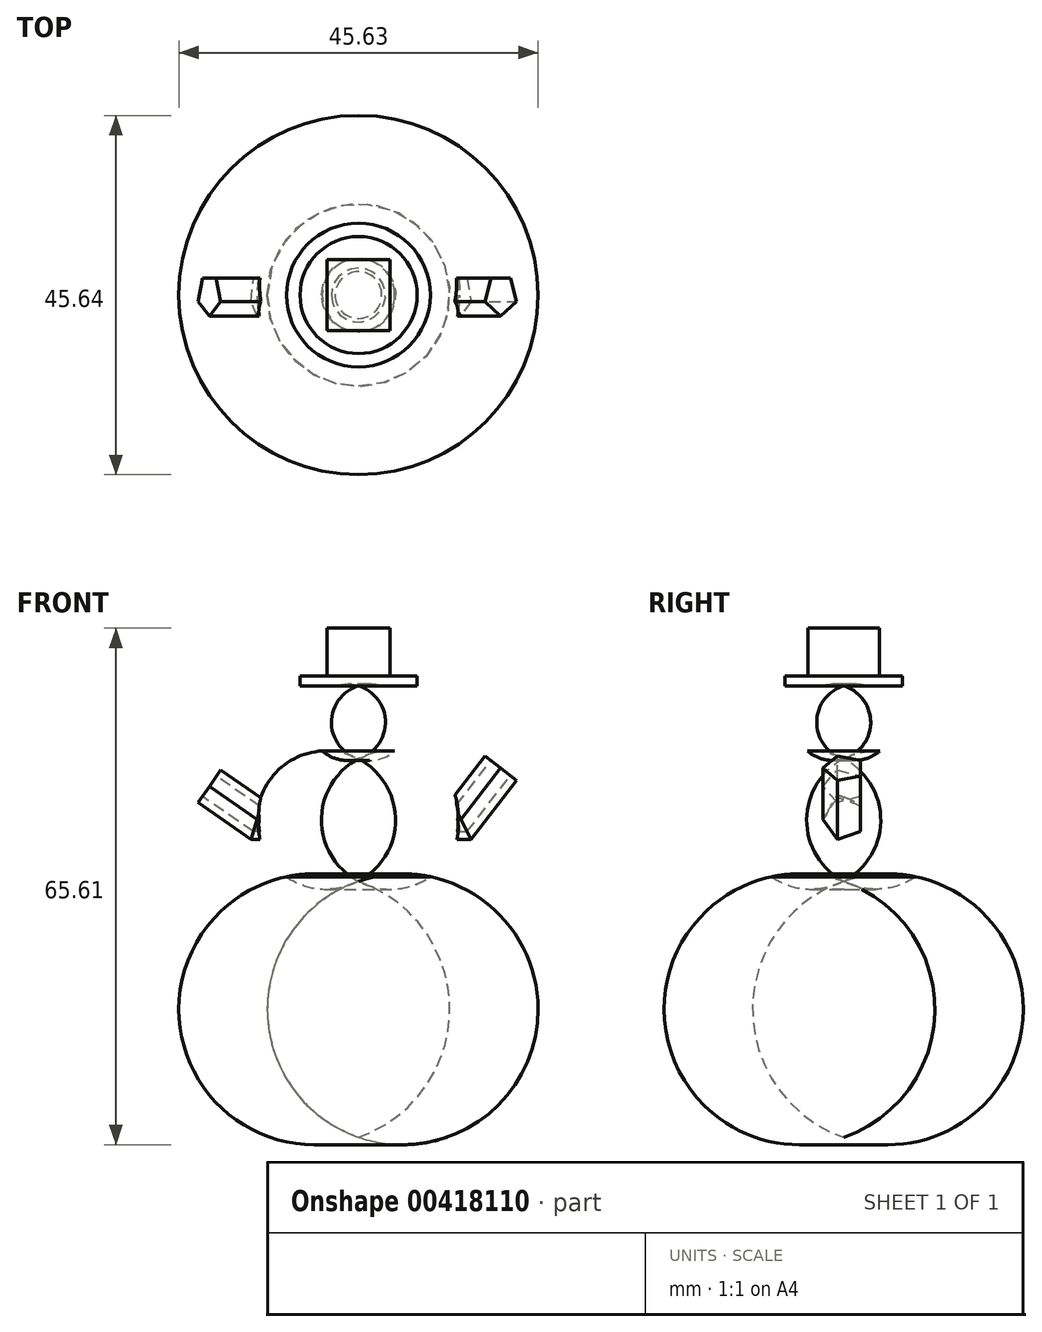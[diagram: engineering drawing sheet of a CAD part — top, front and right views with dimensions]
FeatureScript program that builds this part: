
annotation { "Feature Type Name" : "Feature", "Feature Type Description" : "" }
export const myFeature = defineFeature(function(context is Context, id is Id, definition is map)
    precondition{}
    {
        {
            var Q0;
            Q0=qCreatedBy(makeId("Front.planeOp"),FACE);
            var sketch = newSketch(context, id + "F0", { "sketchPlane" : qUnion([Q0])});
            skLineSegment(sketch, "E0", {"start": v(-0.02, 0.05) * mm, "end": v(-0.02, -57.3) * mm});
            skArc(sketch, "E1", {"start": v(-0.02, 0.05) * mm, "mid": v(-6.28, -4.58) * mm, "end": v(-0.02, -9.21) * mm});
            skArc(sketch, "E2", {"start": v(-0.02, -9.21) * mm, "mid": v(6.23, -4.58) * mm, "end": v(-0.02, 0.05) * mm});
            skArc(sketch, "E3", {"start": v(-0.02, -9.21) * mm, "mid": v(-12.84, -17) * mm, "end": v(-0.02, -24.78) * mm});
            skArc(sketch, "E4", {"start": v(-0.02, -24.78) * mm, "mid": v(12.86, -17) * mm, "end": v(-0.02, -9.21) * mm});
            skArc(sketch, "E5", {"start": v(-0.02, -24.78) * mm, "mid": v(-22.98, -41.04) * mm, "end": v(-0.02, -57.3) * mm});
            skArc(sketch, "E6", {"start": v(-0.02, -57.3) * mm, "mid": v(22.8, -41.04) * mm, "end": v(-0.02, -24.78) * mm});
            skSolve(sketch);
        }
        {
            var Q0;
            {var subQ0=sQuery(id+"F0.wireOp",EDGE,"E4");var subQ2=sQuery(id+"F0.wireOp",EDGE,"E2");var subQ7=makeQuery(id+"F0.imprint","INTERSECT",VERTEX,{"derivedFrom":[subQ2,subQ0]});Q0=makeQuery(id+"F0.imprint","IMPRINT",FACE,{"disambiguationData":[TD([[makeQuery(id+"F0.imprint","IMPRINT",EDGE,{"disambiguationData":[TD([[subQ7,1.0]])],"derivedFrom":subQ0}),1.0]])]});}
            var Q1;
            Q1=sQuery(id+"F0.wireOp",EDGE,"E0");
            revolve(context, id + "F1", {"entities" : qUnion([Q0]), "axis" : qUnion([Q1]), "revolveType" : RevolveType.FULL});
        }
        {
            var Q0;
            {var subQ0=sQuery(id+"F0.wireOp",EDGE,"E2");var subQ4=sQuery(id+"F0.wireOp",EDGE,"E4");var subQ6=makeQuery(id+"F0.imprint","INTERSECT",VERTEX,{"derivedFrom":[subQ0,subQ4]});Q0=makeQuery(id+"F0.imprint","IMPRINT",FACE,{"disambiguationData":[TD([[makeQuery(id+"F0.imprint","IMPRINT",EDGE,{"disambiguationData":[TD([[subQ6,-1.0]])],"derivedFrom":subQ0}),1.0]])]});}
            var Q1;
            Q1=sQuery(id+"F0.wireOp",EDGE,"E0");
            revolve(context, id + "F2", {"entities" : qUnion([Q0]), "axis" : qUnion([Q1]), "revolveType" : RevolveType.FULL});
        }
        {
            var Q0;
            {var subQ0=sQuery(id+"F0.wireOp",EDGE,"E6");var subQ4=sQuery(id+"F0.wireOp",EDGE,"E4");var subQ6=makeQuery(id+"F0.imprint","INTERSECT",VERTEX,{"derivedFrom":[subQ4,subQ0]});Q0=makeQuery(id+"F0.imprint","IMPRINT",FACE,{"disambiguationData":[TD([[makeQuery(id+"F0.imprint","IMPRINT",EDGE,{"disambiguationData":[TD([[subQ6,1.0]])],"derivedFrom":subQ0}),1.0]])]});}
            var Q1;
            {var subQ0=sQuery(id+"F0.wireOp",EDGE,"E6");var subQ1=sQuery(id+"F0.wireOp",EDGE,"E4");var subQ3=makeQuery(id+"F0.imprint","INTERSECT",VERTEX,{"derivedFrom":[subQ1,subQ0]});Q1=makeQuery(id+"F0.imprint","IMPRINT",FACE,{"disambiguationData":[TD([[makeQuery(id+"F0.imprint","IMPRINT",EDGE,{"disambiguationData":[TD([[subQ3,1.0]])],"derivedFrom":subQ1}),1.0]])]});}
            var Q2;
            Q2=sQuery(id+"F0.wireOp",EDGE,"E0");
            revolve(context, id + "F3", {"entities" : qUnion([Q0, Q1]), "axis" : qUnion([Q2]), "revolveType" : RevolveType.FULL});
        }
        {
            var Q0;
            Q0=qCreatedBy(makeId("Top.planeOp"),FACE);
            var sketch = newSketch(context, id + "F4", { "sketchPlane" : qUnion([Q0])});
            skCircle(sketch, "E7", {"center": v(0, 0) * mm, "radius": 7.43 * mm});
            skSolve(sketch);
        }
        {
            var Q0;
            Q0=makeQuery(id+"F4.imprint","IMPRINT",FACE,{"disambiguationData":[TD([[makeQuery(id+"F4.imprint","IMPRINT",EDGE,{"derivedFrom":sQuery(id+"F4.wireOp",EDGE,"E7")}),1.0]])]});
            extrude(context, id + "F5", {"entities" : qUnion([Q0]), "operationType" : NewBodyOperationType.ADD, "depth" : 1.27 * mm});
        }
        {
            var Q0;
            Q0=qCreatedBy(makeId("Front.planeOp"),FACE);
            var sketch = newSketch(context, id + "F6", { "sketchPlane" : qUnion([Q0])});
            skLineSegment(sketch, "E8", {"start": v(0, -16.92) * mm, "end": v(-12.88, -16.92) * mm});
            skLineSegment(sketch, "E9", {"start": v(-12.88, -16.92) * mm, "end": v(-18.97, -12.71) * mm});
            skSolve(sketch);
        }
        {
            var Q0;
            Q0=qCreatedBy(makeId("Front.planeOp"),FACE);
            var sketch = newSketch(context, id + "F7", { "sketchPlane" : qUnion([Q0])});
            skLineSegment(sketch, "E10", {"start": v(0, -16.9) * mm, "end": v(13, -16.9) * mm});
            skLineSegment(sketch, "E11", {"start": v(13, -16.9) * mm, "end": v(18.02, -10.41) * mm});
            skSolve(sketch);
        }
        {
            var Q0;
            Q0=makeQuery(id+"F5.opExtrude","CAP_FACE",FACE,{"disambiguationData":[OSD([sQuery(id+"F4.wireOp",EDGE,"E7")])],"isStart":false});
            var sketch = newSketch(context, id + "F8", { "sketchPlane" : qUnion([Q0])});
            skLineSegment(sketch, "E12.bottom", {"start": v(3.99, -4.53) * mm, "end": v(-3.99, -4.53) * mm});
            skLineSegment(sketch, "E12.top", {"start": v(3.99, 4.53) * mm, "end": v(-3.99, 4.53) * mm});
            skLineSegment(sketch, "E12.left", {"start": v(3.99, -4.53) * mm, "end": v(3.99, 4.53) * mm});
            skLineSegment(sketch, "E12.right", {"start": v(-3.99, -4.53) * mm, "end": v(-3.99, 4.53) * mm});
            skPoint(sketch, "E12.middle", {"position": v(0, 0) * mm});
            skSolve(sketch);
        }
        {
            var Q0;
            Q0=makeQuery(id+"F8.imprint","IMPRINT",FACE,{"disambiguationData":[TD([[makeQuery(id+"F8.imprint","IMPRINT",EDGE,{"derivedFrom":sQuery(id+"F8.wireOp",EDGE,"E12.bottom")}),-1.0]])]});
            extrude(context, id + "F9", {"entities" : qUnion([Q0]), "operationType" : NewBodyOperationType.ADD, "depth" : 6.1 * mm});
        }
        {
            var Q0;
            Q0=qCreatedBy(makeId("Right.planeOp"),FACE);
            var sketch = newSketch(context, id + "F10", { "sketchPlane" : qUnion([Q0])});
            skCircle(sketch, "E13.cCircle", {"center": v(0, -16.91) * mm, "radius": 2.15 * mm, "construction": true});
            skLineSegment(sketch, "E13.0", {"start": v(2.15, -15.35) * mm, "end": v(2.15, -18.47) * mm});
            skLineSegment(sketch, "E13.1", {"start": v(2.15, -18.47) * mm, "end": v(-0.82, -19.44) * mm});
            skLineSegment(sketch, "E13.2", {"start": v(-0.82, -19.44) * mm, "end": v(-2.66, -16.91) * mm});
            skLineSegment(sketch, "E13.3", {"start": v(-2.66, -16.91) * mm, "end": v(-0.82, -14.38) * mm});
            skLineSegment(sketch, "E13.4", {"start": v(-0.82, -14.38) * mm, "end": v(2.15, -15.35) * mm});
            skPoint(sketch, "E13.0.midPoint", {"position": v(2.15, -16.91) * mm});
            skSolve(sketch);
        }
        {
            var Q0;
            Q0 = qSketchRegion(id + "F10", true);
            var Q1;
            Q1 = qConstructionFilter(qBodyType(qCreatedBy(id + "F7" ,EDGE), BodyType.WIRE), ConstructionObject.NO);
            sweep(context, id + "F11", {"operationType" : NewBodyOperationType.ADD, "profiles" : qUnion([Q0]), "path" : qUnion([Q1])});
        }
        {
            var Q0;
            Q0 = qSketchRegion(id + "F10", true);
            var Q1;
            Q1 = qConstructionFilter(qBodyType(qCreatedBy(id + "F6" ,EDGE), BodyType.WIRE), ConstructionObject.NO);
            sweep(context, id + "F12", {"operationType" : NewBodyOperationType.ADD, "profiles" : qUnion([Q0]), "path" : qUnion([Q1])});
        }
    });
